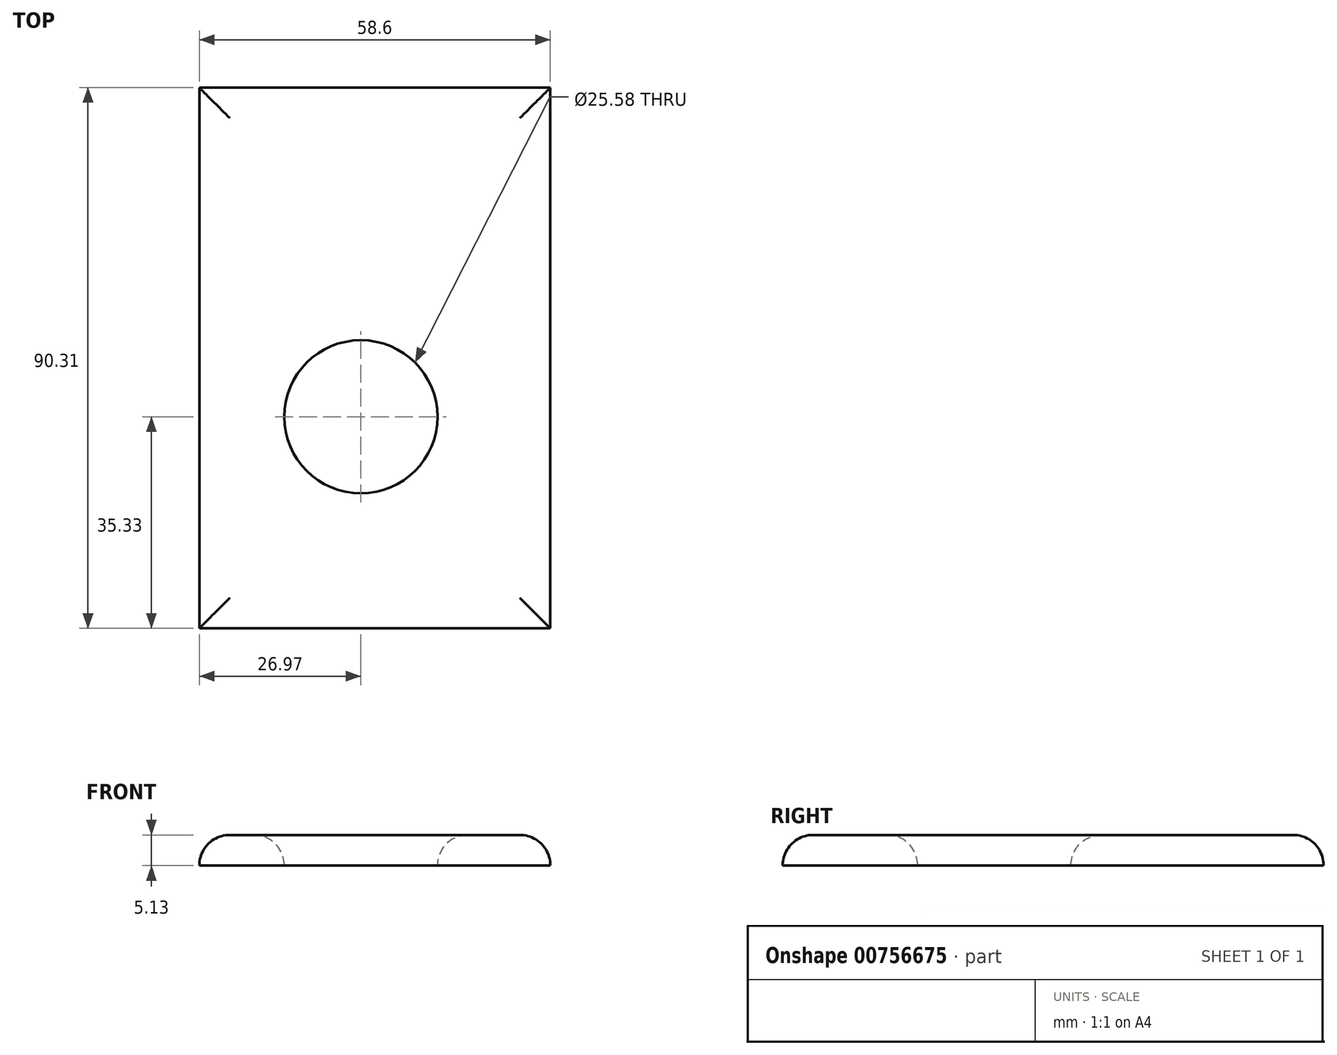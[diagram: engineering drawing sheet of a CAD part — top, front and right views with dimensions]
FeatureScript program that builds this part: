
annotation { "Feature Type Name" : "Feature", "Feature Type Description" : "" }
export const myFeature = defineFeature(function(context is Context, id is Id, definition is map)
    precondition{}
    {
        {
            var Q0;
            Q0=qCreatedBy(makeId("Top.planeOp"),FACE);
            var sketch = newSketch(context, id + "F0", { "sketchPlane" : qUnion([Q0])});
            skLineSegment(sketch, "E0.bottom", {"start": v(0, 54.98) * mm, "end": v(58.6, 54.98) * mm});
            skLineSegment(sketch, "E0.top", {"start": v(0, -35.33) * mm, "end": v(58.6, -35.33) * mm});
            skLineSegment(sketch, "E0.left", {"start": v(0, 54.98) * mm, "end": v(0, -35.33) * mm});
            skLineSegment(sketch, "E0.right", {"start": v(58.6, 54.98) * mm, "end": v(58.6, -35.33) * mm});
            skSolve(sketch);
        }
        {
            var Q0;
            Q0=makeQuery(id+"F0.imprint","IMPRINT",FACE,{"disambiguationData":[TD([[makeQuery(id+"F0.imprint","IMPRINT",EDGE,{"derivedFrom":sQuery(id+"F0.wireOp",EDGE,"E0.bottom")}),-1.0]])]});
            var sketch = newSketch(context, id + "F1", { "sketchPlane" : qUnion([Q0])});
            skCircle(sketch, "E1", {"center": v(26.97, 0) * mm, "radius": 12.8 * mm});
            skSolve(sketch);
        }
        {
            var Q0;
            Q0=makeQuery(id+"F1.imprint","IMPRINT",FACE,{"disambiguationData":[TD([[makeQuery(id+"F1.imprint","IMPRINT",EDGE,{"derivedFrom":sQuery(id+"F1.wireOp",EDGE,"E1")}),-1.0]])]});
            extrude(context, id + "F2", {"entities" : qUnion([Q0]), "depth" : 5.13 * mm, "offsetDistance" : 25.4 * mm});
        }
        {
            var Q0;
            Q0=makeQuery(id+"F2.opExtrude","CAP_FACE",FACE,{"disambiguationData":[OSD([sQuery(id+"F0.wireOp",EDGE,"E0.bottom"),sQuery(id+"F0.wireOp",EDGE,"E0.top"),sQuery(id+"F0.wireOp",EDGE,"E0.left"),sQuery(id+"F0.wireOp",EDGE,"E0.right"),sQuery(id+"F1.wireOp",EDGE,"E1")])],"isStart":false});
            fillet(context, id + "F3", {"entities" : qUnion([Q0]), "radius" : 5.08 * mm, "tangentPropagation" : true, "allowEdgeOverflow" : false});
        }
    });
